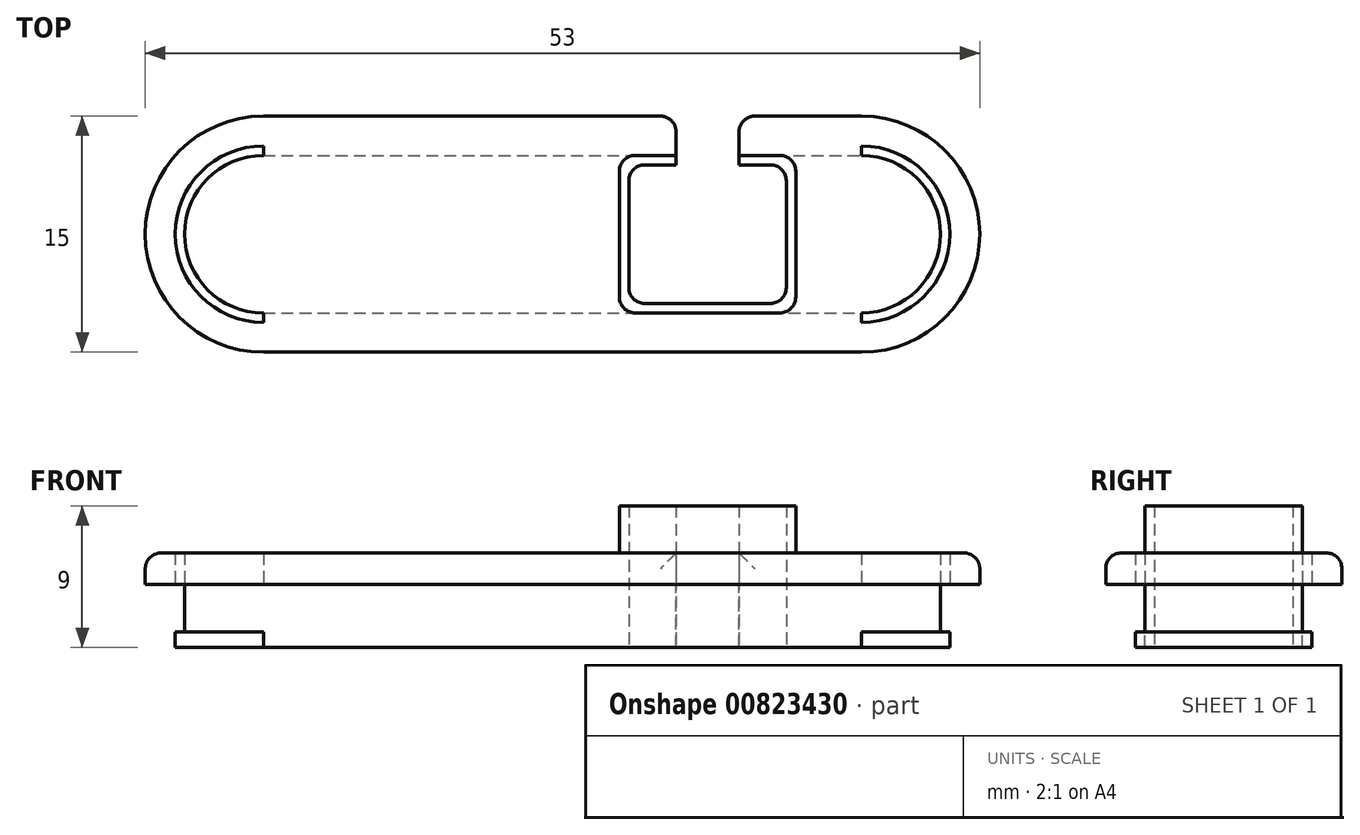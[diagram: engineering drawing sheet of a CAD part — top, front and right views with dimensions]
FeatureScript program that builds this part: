
annotation { "Feature Type Name" : "Feature", "Feature Type Description" : "" }
export const myFeature = defineFeature(function(context is Context, id is Id, definition is map)
    precondition{}
    {
        {
            var Q0;
            Q0=qCreatedBy(makeId("Top.planeOp"),FACE);
            var sketch = newSketch(context, id + "F0", { "sketchPlane" : qUnion([Q0])});
            skLineSegment(sketch, "E0", {"start": v(-19, 5) * mm, "end": v(7.21, 5) * mm});
            skLineSegment(sketch, "E1", {"start": v(-19, -5) * mm, "end": v(19, -5) * mm});
            skArc(sketch, "E2", {"start": v(-19, 5) * mm, "mid": v(-24, 0) * mm, "end": v(-19, -5) * mm});
            skArc(sketch, "E3", {"start": v(19, -5) * mm, "mid": v(24, 0) * mm, "end": v(19, 5) * mm});
            skLineSegment(sketch, "E4.0", {"start": v(-19, 5.6) * mm, "end": v(7.21, 5.6) * mm});
            skArc(sketch, "E4.1", {"start": v(-19, 5.6) * mm, "mid": v(-24.6, 0) * mm, "end": v(-19, -5.6) * mm});
            skLineSegment(sketch, "E4.2", {"start": v(-19, -5.6) * mm, "end": v(19, -5.6) * mm});
            skArc(sketch, "E4.3", {"start": v(19, -5.6) * mm, "mid": v(24.6, 0) * mm, "end": v(19, 5.6) * mm});
            skLineSegment(sketch, "E5.0", {"start": v(-19, 7.5) * mm, "end": v(7.21, 7.5) * mm});
            skArc(sketch, "E5.1", {"start": v(-19, 7.5) * mm, "mid": v(-26.5, 0) * mm, "end": v(-19, -7.5) * mm});
            skLineSegment(sketch, "E5.2", {"start": v(-19, -7.5) * mm, "end": v(19, -7.5) * mm});
            skArc(sketch, "E5.3", {"start": v(19, -7.5) * mm, "mid": v(26.5, 0) * mm, "end": v(19, 7.5) * mm});
            skLineSegment(sketch, "E6", {"start": v(3.61, 5) * mm, "end": v(3.61, -5) * mm});
            skLineSegment(sketch, "E7", {"start": v(14.81, 5) * mm, "end": v(14.81, -5) * mm});
            skLineSegment(sketch, "E8", {"start": v(4.21, 5) * mm, "end": v(4.21, -5) * mm});
            skLineSegment(sketch, "E9", {"start": v(14.21, 5) * mm, "end": v(14.21, -5) * mm});
            skLineSegment(sketch, "E10", {"start": v(3.61, 5) * mm, "end": v(3.61, 5.6) * mm});
            skLineSegment(sketch, "E11", {"start": v(14.81, 5) * mm, "end": v(14.81, 5.6) * mm});
            skLineSegment(sketch, "E12", {"start": v(3.61, -5) * mm, "end": v(3.61, -5.6) * mm});
            skLineSegment(sketch, "E13", {"start": v(14.81, -5) * mm, "end": v(14.81, -5.6) * mm});
            skLineSegment(sketch, "E14", {"start": v(7.21, 5) * mm, "end": v(7.21, 5.6) * mm});
            skLineSegment(sketch, "E15", {"start": v(7.21, 5.6) * mm, "end": v(7.21, 7.5) * mm});
            skLineSegment(sketch, "E16", {"start": v(11.21, 5) * mm, "end": v(11.21, 5.6) * mm});
            skLineSegment(sketch, "E17", {"start": v(11.21, 5.6) * mm, "end": v(11.21, 7.5) * mm});
            skLineSegment(sketch, "E18.trimOffspring", {"start": v(11.21, 7.5) * mm, "end": v(19, 7.5) * mm});
            skLineSegment(sketch, "E19.trimOffspring", {"start": v(11.21, 5.6) * mm, "end": v(19, 5.6) * mm});
            skLineSegment(sketch, "E20.trimOffspring", {"start": v(11.21, 5) * mm, "end": v(19, 5) * mm});
            skLineSegment(sketch, "E21", {"start": v(19, 5.6) * mm, "end": v(19, 5) * mm});
            skLineSegment(sketch, "E22", {"start": v(19, -5) * mm, "end": v(19, -5.6) * mm});
            skLineSegment(sketch, "E23", {"start": v(-19, 5.6) * mm, "end": v(-19, 5) * mm});
            skLineSegment(sketch, "E24", {"start": v(-19, -5) * mm, "end": v(-19, -5.6) * mm});
            skLineSegment(sketch, "E25", {"start": v(4.21, -4.4) * mm, "end": v(14.21, -4.4) * mm});
            skLineSegment(sketch, "E26", {"start": v(4.21, 4.4) * mm, "end": v(7.21, 4.4) * mm});
            skLineSegment(sketch, "E27", {"start": v(7.21, 5) * mm, "end": v(7.21, 4.4) * mm});
            skLineSegment(sketch, "E28", {"start": v(11.21, 5) * mm, "end": v(11.21, 4.4) * mm});
            skLineSegment(sketch, "E29.trimOffspring", {"start": v(11.21, 4.4) * mm, "end": v(14.21, 4.4) * mm});
            skSolve(sketch);
        }
        {
            var Q0;
            {var subQ4=sQuery(id+"F0.wireOp",EDGE,"E4.1");Q0=makeQuery(id+"F0.imprint","IMPRINT",FACE,{"disambiguationData":[TD([[makeQuery(id+"F0.imprint","IMPRINT",EDGE,{"derivedFrom":subQ4}),-1.0]])]});}
            var Q1;
            {var subQ2=sQuery(id+"F0.wireOp",EDGE,"E10");Q1=makeQuery(id+"F0.imprint","IMPRINT",FACE,{"disambiguationData":[TD([[makeQuery(id+"F0.imprint","IMPRINT",EDGE,{"derivedFrom":subQ2}),1.0]])]});}
            var Q2;
            {var subQ0=sQuery(id+"F0.wireOp",EDGE,"E11");Q2=makeQuery(id+"F0.imprint","IMPRINT",FACE,{"disambiguationData":[TD([[makeQuery(id+"F0.imprint","IMPRINT",EDGE,{"derivedFrom":subQ0}),-1.0]])]});}
            var Q3;
            {var subQ2=sQuery(id+"F0.wireOp",EDGE,"E12");Q3=makeQuery(id+"F0.imprint","IMPRINT",FACE,{"disambiguationData":[TD([[makeQuery(id+"F0.imprint","IMPRINT",EDGE,{"derivedFrom":subQ2}),-1.0]])]});}
            var Q4;
            {var subQ2=sQuery(id+"F0.wireOp",EDGE,"E13");Q4=makeQuery(id+"F0.imprint","IMPRINT",FACE,{"disambiguationData":[TD([[makeQuery(id+"F0.imprint","IMPRINT",EDGE,{"derivedFrom":subQ2}),1.0]])]});}
            var Q5;
            {var subQ0=sQuery(id+"F0.wireOp",EDGE,"E2");Q5=makeQuery(id+"F0.imprint","IMPRINT",FACE,{"disambiguationData":[TD([[makeQuery(id+"F0.imprint","IMPRINT",EDGE,{"derivedFrom":subQ0}),1.0]])]});}
            var Q6;
            {var subQ0=sQuery(id+"F0.wireOp",EDGE,"E6");Q6=makeQuery(id+"F0.imprint","IMPRINT",FACE,{"disambiguationData":[TD([[makeQuery(id+"F0.imprint","IMPRINT",EDGE,{"derivedFrom":subQ0}),1.0]])]});}
            var Q7;
            {var subQ0=sQuery(id+"F0.wireOp",EDGE,"E10");Q7=makeQuery(id+"F0.imprint","IMPRINT",FACE,{"disambiguationData":[TD([[makeQuery(id+"F0.imprint","IMPRINT",EDGE,{"derivedFrom":subQ0}),-1.0]])]});}
            var Q8;
            {var subQ0=sQuery(id+"F0.wireOp",EDGE,"E3");Q8=makeQuery(id+"F0.imprint","IMPRINT",FACE,{"disambiguationData":[TD([[makeQuery(id+"F0.imprint","IMPRINT",EDGE,{"derivedFrom":subQ0}),1.0]])]});}
            var Q9;
            {var subQ4=sQuery(id+"F0.wireOp",EDGE,"E12");Q9=makeQuery(id+"F0.imprint","IMPRINT",FACE,{"disambiguationData":[TD([[makeQuery(id+"F0.imprint","IMPRINT",EDGE,{"derivedFrom":subQ4}),1.0]])]});}
            var Q10;
            {var subQ0=sQuery(id+"F0.wireOp",EDGE,"E7");Q10=makeQuery(id+"F0.imprint","IMPRINT",FACE,{"disambiguationData":[TD([[makeQuery(id+"F0.imprint","IMPRINT",EDGE,{"derivedFrom":subQ0}),-1.0]])]});}
            var Q11;
            {var subQ1=sQuery(id+"F0.wireOp",EDGE,"E11");Q11=makeQuery(id+"F0.imprint","IMPRINT",FACE,{"disambiguationData":[TD([[makeQuery(id+"F0.imprint","IMPRINT",EDGE,{"derivedFrom":subQ1}),1.0]])]});}
            var Q12;
            {var subQ5=sQuery(id+"F0.wireOp",EDGE,"E25");Q12=makeQuery(id+"F0.imprint","IMPRINT",FACE,{"disambiguationData":[TD([[makeQuery(id+"F0.imprint","IMPRINT",EDGE,{"derivedFrom":subQ5}),-1.0]])]});}
            var Q13;
            {var subQ4=sQuery(id+"F0.wireOp",EDGE,"E26");Q13=makeQuery(id+"F0.imprint","IMPRINT",FACE,{"disambiguationData":[TD([[makeQuery(id+"F0.imprint","IMPRINT",EDGE,{"derivedFrom":subQ4}),1.0]])]});}
            var Q14;
            {var subQ4=sQuery(id+"F0.wireOp",EDGE,"E28");Q14=makeQuery(id+"F0.imprint","IMPRINT",FACE,{"disambiguationData":[TD([[makeQuery(id+"F0.imprint","IMPRINT",EDGE,{"derivedFrom":subQ4}),1.0]])]});}
            extrude(context, id + "F1", {"entities" : qUnion([Q0, Q1, Q2, Q3, Q4, Q5, Q6, Q7, Q8, Q9, Q10, Q11, Q12, Q13, Q14]), "depth" : 2 * mm, "offsetDistance" : 25 * mm});
        }
        {
            var Q0;
            {var subQ0=sQuery(id+"F0.wireOp",EDGE,"E2");Q0=makeQuery(id+"F0.imprint","IMPRINT",FACE,{"disambiguationData":[TD([[makeQuery(id+"F0.imprint","IMPRINT",EDGE,{"derivedFrom":subQ0}),1.0]])]});}
            var Q1;
            {var subQ0=sQuery(id+"F0.wireOp",EDGE,"E3");Q1=makeQuery(id+"F0.imprint","IMPRINT",FACE,{"disambiguationData":[TD([[makeQuery(id+"F0.imprint","IMPRINT",EDGE,{"derivedFrom":subQ0}),1.0]])]});}
            var Q2;
            {var subQ0=sQuery(id+"F0.wireOp",EDGE,"E6");Q2=makeQuery(id+"F0.imprint","IMPRINT",FACE,{"disambiguationData":[TD([[makeQuery(id+"F0.imprint","IMPRINT",EDGE,{"derivedFrom":subQ0}),1.0]])]});}
            var Q3;
            {var subQ0=sQuery(id+"F0.wireOp",EDGE,"E7");Q3=makeQuery(id+"F0.imprint","IMPRINT",FACE,{"disambiguationData":[TD([[makeQuery(id+"F0.imprint","IMPRINT",EDGE,{"derivedFrom":subQ0}),-1.0]])]});}
            var Q4;
            {var subQ5=sQuery(id+"F0.wireOp",EDGE,"E25");Q4=makeQuery(id+"F0.imprint","IMPRINT",FACE,{"disambiguationData":[TD([[makeQuery(id+"F0.imprint","IMPRINT",EDGE,{"derivedFrom":subQ5}),-1.0]])]});}
            var Q5;
            {var subQ4=sQuery(id+"F0.wireOp",EDGE,"E26");Q5=makeQuery(id+"F0.imprint","IMPRINT",FACE,{"disambiguationData":[TD([[makeQuery(id+"F0.imprint","IMPRINT",EDGE,{"derivedFrom":subQ4}),1.0]])]});}
            var Q6;
            {var subQ4=sQuery(id+"F0.wireOp",EDGE,"E28");Q6=makeQuery(id+"F0.imprint","IMPRINT",FACE,{"disambiguationData":[TD([[makeQuery(id+"F0.imprint","IMPRINT",EDGE,{"derivedFrom":subQ4}),1.0]])]});}
            extrude(context, id + "F2", {"entities" : qUnion([Q0, Q1, Q2, Q3, Q4, Q5, Q6]), "operationType" : NewBodyOperationType.ADD, "depth" : -4 * mm, "offsetDistance" : 25 * mm});
        }
        {
            var Q0;
            Q0=makeQuery(id+"F0.imprint","IMPRINT",FACE,{"disambiguationData":[TD([[makeQuery(id+"F0.imprint","IMPRINT",EDGE,{"derivedFrom":sQuery(id+"F0.wireOp",EDGE,"E2")}),-1.0]])]});
            var Q1;
            Q1=makeQuery(id+"F0.imprint","IMPRINT",FACE,{"disambiguationData":[TD([[makeQuery(id+"F0.imprint","IMPRINT",EDGE,{"derivedFrom":sQuery(id+"F0.wireOp",EDGE,"E3")}),-1.0]])]});
            extrude(context, id + "F3", {"entities" : qUnion([Q0, Q1]), "operationType" : NewBodyOperationType.ADD, "oppositeDirection" : true, "depth" : 4 * mm, "offsetDistance" : 25 * mm, "hasSecondDirection" : true, "secondDirectionOppositeDirection" : true, "secondDirectionDepth" : 3 * mm});
        }
        {
            var Q0;
            {var subQ0=sQuery(id+"F0.wireOp",EDGE,"E6");Q0=makeQuery(id+"F0.imprint","IMPRINT",FACE,{"disambiguationData":[TD([[makeQuery(id+"F0.imprint","IMPRINT",EDGE,{"derivedFrom":subQ0}),1.0]])]});}
            var Q1;
            {var subQ0=sQuery(id+"F0.wireOp",EDGE,"E7");Q1=makeQuery(id+"F0.imprint","IMPRINT",FACE,{"disambiguationData":[TD([[makeQuery(id+"F0.imprint","IMPRINT",EDGE,{"derivedFrom":subQ0}),-1.0]])]});}
            var Q2;
            {var subQ5=sQuery(id+"F0.wireOp",EDGE,"E25");Q2=makeQuery(id+"F0.imprint","IMPRINT",FACE,{"disambiguationData":[TD([[makeQuery(id+"F0.imprint","IMPRINT",EDGE,{"derivedFrom":subQ5}),-1.0]])]});}
            var Q3;
            {var subQ4=sQuery(id+"F0.wireOp",EDGE,"E26");Q3=makeQuery(id+"F0.imprint","IMPRINT",FACE,{"disambiguationData":[TD([[makeQuery(id+"F0.imprint","IMPRINT",EDGE,{"derivedFrom":subQ4}),1.0]])]});}
            var Q4;
            {var subQ4=sQuery(id+"F0.wireOp",EDGE,"E28");Q4=makeQuery(id+"F0.imprint","IMPRINT",FACE,{"disambiguationData":[TD([[makeQuery(id+"F0.imprint","IMPRINT",EDGE,{"derivedFrom":subQ4}),1.0]])]});}
            extrude(context, id + "F4", {"entities" : qUnion([Q0, Q1, Q2, Q3, Q4]), "operationType" : NewBodyOperationType.ADD, "depth" : 5 * mm, "offsetDistance" : 25 * mm});
        }
        {
            var Q0;
            Q0=makeQuery(id+"F1.opExtrude","SWEPT_EDGE",EDGE,{"disambiguationData":[OSD([sQuery(id+"F0.wireOp",EDGE,"E17"),sQuery(id+"F0.wireOp",EDGE,"E18.trimOffspring")])]});
            var Q1;
            Q1=makeQuery(id+"F1.opExtrude","SWEPT_EDGE",EDGE,{"disambiguationData":[OSD([sQuery(id+"F0.wireOp",EDGE,"E5.0"),sQuery(id+"F0.wireOp",EDGE,"E15")])]});
            var Q2;
            Q2=makeQuery(id+"F1.opExtrude","CAP_EDGE",EDGE,{"disambiguationData":[OSD([sQuery(id+"F0.wireOp",EDGE,"E5.2")])],"isStart":false});
            var Q3;
            {var subQ0=sQuery(id+"F0.wireOp",EDGE,"E25");var subQ1=sQuery(id+"F0.wireOp",EDGE,"E8");Q3=makeQuery(id+"F4.boolean.opBoolean","MERGE",EDGE,{"derivedFrom":[makeQuery(id+"F2.boolean.opBoolean","MERGE",EDGE,{"derivedFrom":[makeQuery(id+"F1.opExtrude","SWEPT_EDGE",EDGE,{"disambiguationData":[OSD([subQ1,subQ0])]}),makeQuery(id+"F2.opExtrude","SWEPT_EDGE",EDGE,{"disambiguationData":[OSD([subQ1,subQ0])]})]}),makeQuery(id+"F4.opExtrude","SWEPT_EDGE",EDGE,{"disambiguationData":[OSD([subQ1,subQ0])]})]});}
            var Q4;
            {var subQ0=sQuery(id+"F0.wireOp",EDGE,"E25");var subQ1=sQuery(id+"F0.wireOp",EDGE,"E9");Q4=makeQuery(id+"F4.boolean.opBoolean","MERGE",EDGE,{"derivedFrom":[makeQuery(id+"F2.boolean.opBoolean","MERGE",EDGE,{"derivedFrom":[makeQuery(id+"F1.opExtrude","SWEPT_EDGE",EDGE,{"disambiguationData":[OSD([subQ1,subQ0])]}),makeQuery(id+"F2.opExtrude","SWEPT_EDGE",EDGE,{"disambiguationData":[OSD([subQ1,subQ0])]})]}),makeQuery(id+"F4.opExtrude","SWEPT_EDGE",EDGE,{"disambiguationData":[OSD([subQ1,subQ0])]})]});}
            var Q5;
            Q5=makeQuery(id+"F4.opExtrude","SWEPT_EDGE",EDGE,{"disambiguationData":[OSD([sQuery(id+"F0.wireOp",EDGE,"E1"),sQuery(id+"F0.wireOp",EDGE,"E6"),sQuery(id+"F0.wireOp",EDGE,"E12")])]});
            var Q6;
            Q6=makeQuery(id+"F4.opExtrude","SWEPT_EDGE",EDGE,{"disambiguationData":[OSD([sQuery(id+"F0.wireOp",EDGE,"E1"),sQuery(id+"F0.wireOp",EDGE,"E7"),sQuery(id+"F0.wireOp",EDGE,"E13")])]});
            var Q7;
            Q7=makeQuery(id+"F4.opExtrude","SWEPT_EDGE",EDGE,{"disambiguationData":[OSD([sQuery(id+"F0.wireOp",EDGE,"E7"),sQuery(id+"F0.wireOp",EDGE,"E11"),sQuery(id+"F0.wireOp",EDGE,"E20.trimOffspring")])]});
            var Q8;
            Q8=makeQuery(id+"F4.opExtrude","SWEPT_EDGE",EDGE,{"disambiguationData":[OSD([sQuery(id+"F0.wireOp",EDGE,"E0"),sQuery(id+"F0.wireOp",EDGE,"E6"),sQuery(id+"F0.wireOp",EDGE,"E10")])]});
            var Q9;
            {var subQ0=sQuery(id+"F0.wireOp",EDGE,"E26");var subQ1=sQuery(id+"F0.wireOp",EDGE,"E8");Q9=makeQuery(id+"F4.boolean.opBoolean","MERGE",EDGE,{"derivedFrom":[makeQuery(id+"F2.boolean.opBoolean","MERGE",EDGE,{"derivedFrom":[makeQuery(id+"F1.opExtrude","SWEPT_EDGE",EDGE,{"disambiguationData":[OSD([subQ1,subQ0])]}),makeQuery(id+"F2.opExtrude","SWEPT_EDGE",EDGE,{"disambiguationData":[OSD([subQ1,subQ0])]})]}),makeQuery(id+"F4.opExtrude","SWEPT_EDGE",EDGE,{"disambiguationData":[OSD([subQ1,subQ0])]})]});}
            var Q10;
            {var subQ0=sQuery(id+"F0.wireOp",EDGE,"E29.trimOffspring");var subQ1=sQuery(id+"F0.wireOp",EDGE,"E9");Q10=makeQuery(id+"F4.boolean.opBoolean","MERGE",EDGE,{"derivedFrom":[makeQuery(id+"F2.boolean.opBoolean","MERGE",EDGE,{"derivedFrom":[makeQuery(id+"F1.opExtrude","SWEPT_EDGE",EDGE,{"disambiguationData":[OSD([subQ1,subQ0])]}),makeQuery(id+"F2.opExtrude","SWEPT_EDGE",EDGE,{"disambiguationData":[OSD([subQ1,subQ0])]})]}),makeQuery(id+"F4.opExtrude","SWEPT_EDGE",EDGE,{"disambiguationData":[OSD([subQ1,subQ0])]})]});}
            fillet(context, id + "F5", {"entities" : qUnion([Q0, Q1, Q2, Q3, Q4, Q5, Q6, Q7, Q8, Q9, Q10]), "radius" : 1 * mm, "tangentPropagation" : true, "allowEdgeOverflow" : false});
        }
    });
